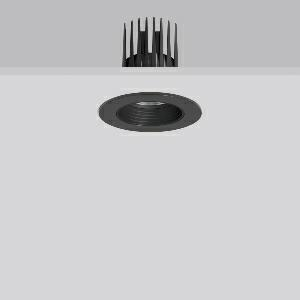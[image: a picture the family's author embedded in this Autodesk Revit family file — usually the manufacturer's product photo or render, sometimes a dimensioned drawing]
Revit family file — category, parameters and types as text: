
# Revit family: heledon_mini_e_901746_003_3_76_8db9
name_source: partatom
category: Lighting Fixtures
units: mm (PartAtom-declared; Revit-internal decimal feet)

## family parameters
Cut with Voids When Loaded = No
Host = Face
Light Source = No
Part Type = Normal
Room Calculation Point = No
Round Connector Dimension = Use Diameter
Shared = No

## types (1)
- HELEDON mini E (1 x LED Modul 935, 2300 lm, 3500)
    Apparent Load = 20 VA
    Approval mark = CE
    CIE Flux Codes = 80 99 100 100 100
    Color Rendering = 92
    Color Temperature = 3500
    Default Elevation = 1800 mm
    Description = Series: HELEDON mini
Round recessed downlight. Housing: die-cast aluminium, powder-coated. Black plastic ring and recessed LED to prevent glare from the side. Optical assembly with lens made of plastic (polycarbonate) for the best homogeneous light distribution - can be changed without tools. Best colour rendering index Ra>90. Suitable for Recessed ceiling mounting. Installation without tools thanks to spring fastening system. Including separate LED converter with connecting cable 600 mm.High quality converter without flickering and stroboscopic effect. Through-wiring box (5 pole) available as accessory. The following accessories can be mounted without use of tools: interchangeable lenses, decorative glasses, honeycomb louvre, clear and frosted diffusers, white interchangeable plastic ring. 
Colour: deep black, matt (RAL 9005)
Diameter: 124 mm
Height: 3 mm
Cut-out diameter: 114 mm
Recess height: 170 mm
Luminaire: recess height: 120 mm
Lamp: LED
Socket: without socket
Colour temperature: 3500K
Colour rendering index (CRI): 92
System power: 20 W
Rated luminous flux: 2300 lm
Luminous efficiency: 115 lm/W
Control gear: Converter, dimmable, DALI
Protection class: II
Type of protection: IP 20
    Height = 0 mm  [stored 0 ft]
    Lamp = 1 x LED Modul 935
    Lamp Light Flux = 2300 lm
    Lamp count = 1
    Length = 124 mm  [stored 0.406824 ft]
    Lifetime = 50000 h
    Luminous efficacy = 115 lm/W
    Manufacturer = RZB
    ModVariant = No
    Model = 901746.003.3.76
    Mounting Place = Ceiling
    Mounting Type = Recessed
    Number of Poles = 1
    OnlyDefault = Yes
    Power Factor = 1
    Product Name = HELEDON mini E
    Product group = Recessed downlights
    ProductGroupID = 402
    Protection Class = Protection class II
    Protection Degree = IP 20
    RLX_Detail_Level = 1
    RLX_Emergency_Light_Flux = 0 lm
    RLX_Emergency_Type = 0
    RLX_Emergency_Type_DB = No
    RlxData = <blob elided: 125589 chars, md5=ec4cf1a6>
    Socket = socket
    Standby Power = 0 W
    System Light Flux = 2300 lm
    System Power = 20 W
    Type Comments = Product without accessories
    Type Image = 901656.003.jpg
    URL = http://relux.com
    VarID = ---
    Voltage = 230 V
    Voltage Range = 220-240 V
    Weight = 0.00 kg
    Width = 0 mm  [stored 0 ft]

note: [stored X ft] marks values corroborated as IEEE doubles in the binary element streams (Revit-internal decimal feet)

## geometry (parser evidence)
native form markers: Blend x4, Sweep x10
no freeform markers — native parametric forms only
